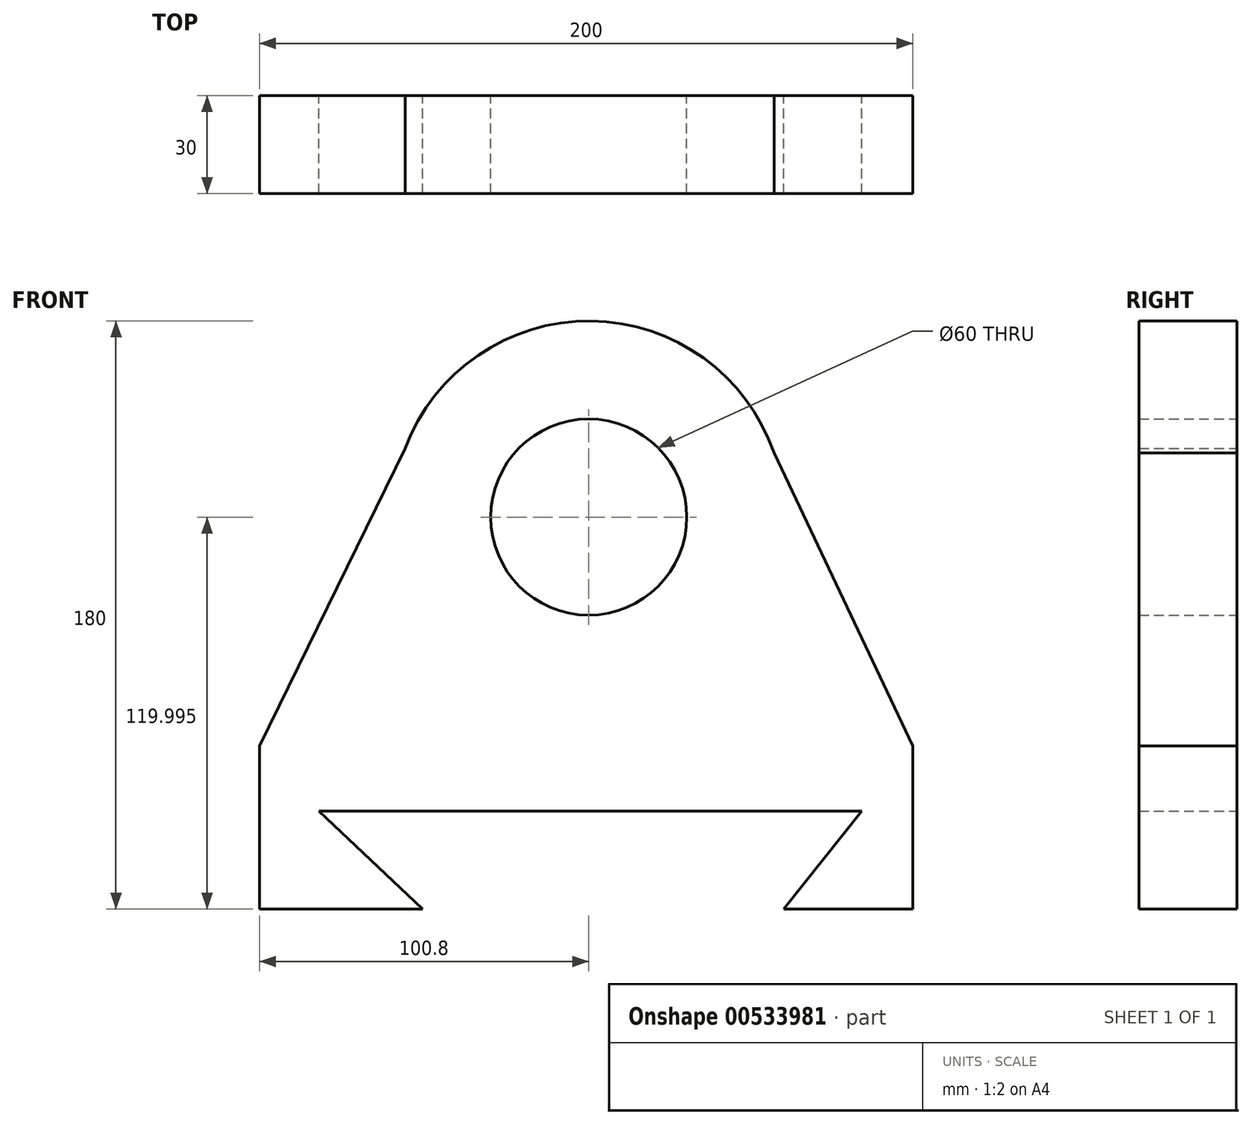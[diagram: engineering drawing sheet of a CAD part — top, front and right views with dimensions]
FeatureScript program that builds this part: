
annotation { "Feature Type Name" : "Feature", "Feature Type Description" : "" }
export const myFeature = defineFeature(function(context is Context, id is Id, definition is map)
    precondition{}
    {
        {
            var Q0;
            Q0=qCreatedBy(makeId("Front.planeOp"),FACE);
            var sketch = newSketch(context, id + "F0", { "sketchPlane" : qUnion([Q0])});
            skLineSegment(sketch, "E0", {"start": v(-100.8, -8.01) * mm, "end": v(99.2, -8.01) * mm});
            skLineSegment(sketch, "E1", {"start": v(-100.8, -8.01) * mm, "end": v(-100.8, -58.01) * mm});
            skLineSegment(sketch, "E2", {"start": v(-100.8, -58.01) * mm, "end": v(-50.8, -58.01) * mm});
            skLineSegment(sketch, "E3", {"start": v(-50.8, -58.01) * mm, "end": v(-82.6, -28.01) * mm});
            skLineSegment(sketch, "E4", {"start": v(-82.6, -28.01) * mm, "end": v(83.6, -28.01) * mm});
            skLineSegment(sketch, "E5", {"start": v(83.6, -28.01) * mm, "end": v(59.6, -58.01) * mm});
            skLineSegment(sketch, "E6", {"start": v(59.6, -58.01) * mm, "end": v(99.2, -58.01) * mm});
            skLineSegment(sketch, "E7", {"start": v(99.2, -58.01) * mm, "end": v(99.2, -8.01) * mm});
            skCircle(sketch, "E8", {"center": v(0, 61.99) * mm, "radius": 30 * mm});
            skCircle(sketch, "E9", {"center": v(0, 61.99) * mm, "radius": 60 * mm});
            skLineSegment(sketch, "E10", {"start": v(-100.8, -8.01) * mm, "end": v(-51.07, 93.49) * mm});
            skLineSegment(sketch, "E11", {"start": v(99.2, -8.01) * mm, "end": v(51.07, 93.49) * mm});
            skSolve(sketch);
        }
        {
            var Q0;
            Q0 = qSketchRegion(id + "F0", true);
            extrude(context, id + "F1", {"entities" : qUnion([Q0]), "depth" : 25 * mm, "offsetDistance" : 25 * mm});
        }
        {
            var Q0;
            Q0 = qSketchRegion(id + "F0", true);
            extrude(context, id + "F2", {"entities" : qUnion([Q0]), "operationType" : NewBodyOperationType.ADD, "depth" : 30 * mm, "offsetDistance" : 25 * mm});
        }
    });
